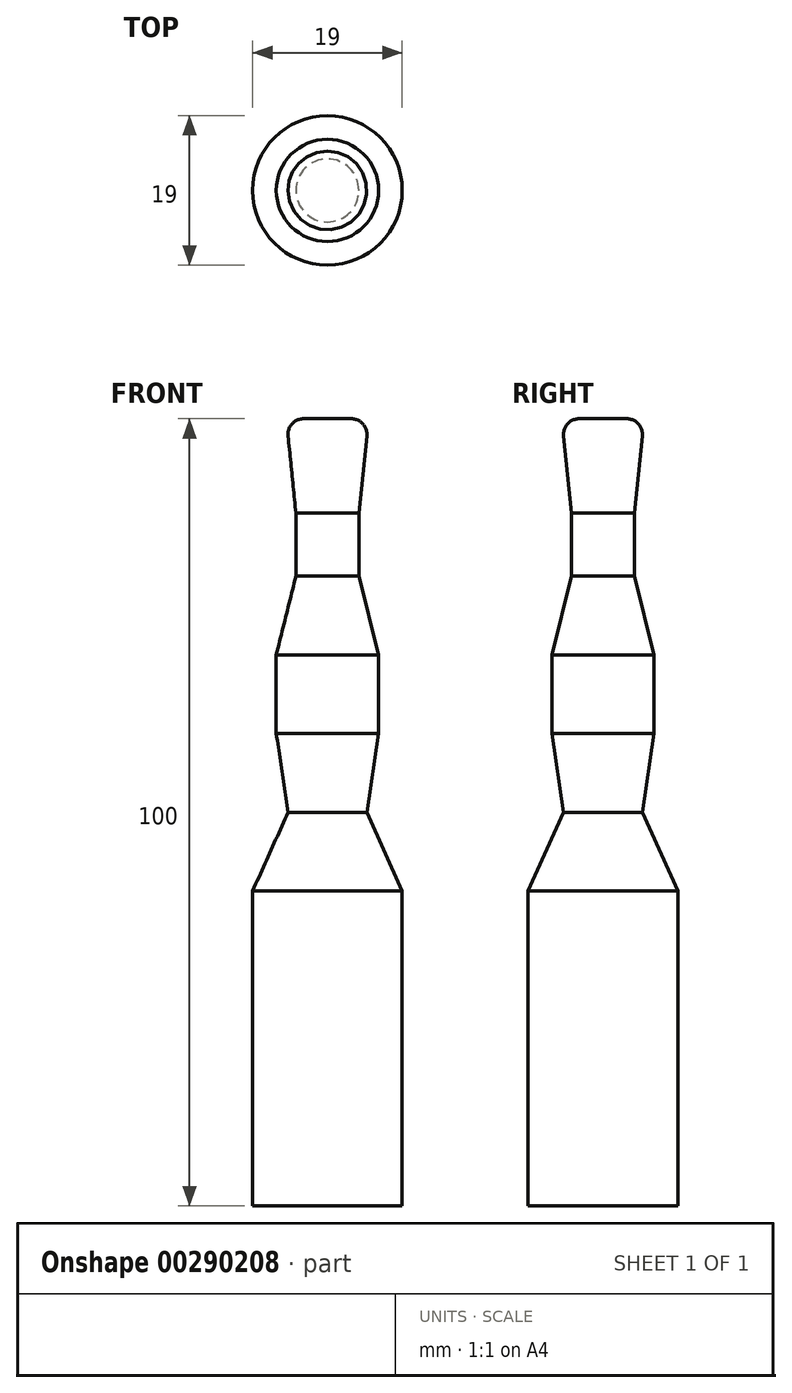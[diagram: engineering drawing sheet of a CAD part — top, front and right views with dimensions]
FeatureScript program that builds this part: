
annotation { "Feature Type Name" : "Feature", "Feature Type Description" : "" }
export const myFeature = defineFeature(function(context is Context, id is Id, definition is map)
    precondition{}
    {
        {
            var Q0;
            Q0=qCreatedBy(makeId("Front.planeOp"),FACE);
            var sketch = newSketch(context, id + "F0", { "sketchPlane" : qUnion([Q0])});
            skLineSegment(sketch, "E0", {"start": v(0, 0) * mm, "end": v(3.01, 0) * mm});
            skArc(sketch, "E1", {"start": v(5, -2.2) * mm, "mid": v(4.5, -0.66) * mm, "end": v(3.01, 0) * mm});
            skLineSegment(sketch, "E2", {"start": v(5, -2.2) * mm, "end": v(4, -12) * mm});
            skLineSegment(sketch, "E3", {"start": v(4, -12) * mm, "end": v(4, -20) * mm});
            skLineSegment(sketch, "E4", {"start": v(4, -20) * mm, "end": v(6.5, -30) * mm});
            skLineSegment(sketch, "E5", {"start": v(6.5, -30) * mm, "end": v(6.5, -40) * mm});
            skLineSegment(sketch, "E6", {"start": v(6.5, -40) * mm, "end": v(5, -50) * mm});
            skLineSegment(sketch, "E7", {"start": v(9.5, -60) * mm, "end": v(9.5, -100) * mm});
            skLineSegment(sketch, "E8", {"start": v(9.5, -100) * mm, "end": v(0, -100) * mm});
            skLineSegment(sketch, "E9", {"start": v(0, -100) * mm, "end": v(0, 0) * mm});
            skLineSegment(sketch, "E10", {"start": v(5, -50) * mm, "end": v(9.5, -60) * mm});
            skSolve(sketch);
        }
        {
            var Q0;
            Q0=makeQuery(id+"F0.imprint","IMPRINT",FACE,{"disambiguationData":[TD([[makeQuery(id+"F0.imprint","IMPRINT",EDGE,{"derivedFrom":sQuery(id+"F0.wireOp",EDGE,"E0")}),-1.0]])]});
            var Q1;
            Q1=sQuery(id+"F0.wireOp",EDGE,"E9");
            revolve(context, id + "F1", {"entities" : qUnion([Q0]), "axis" : qUnion([Q1]), "revolveType" : RevolveType.FULL});
        }
    });
